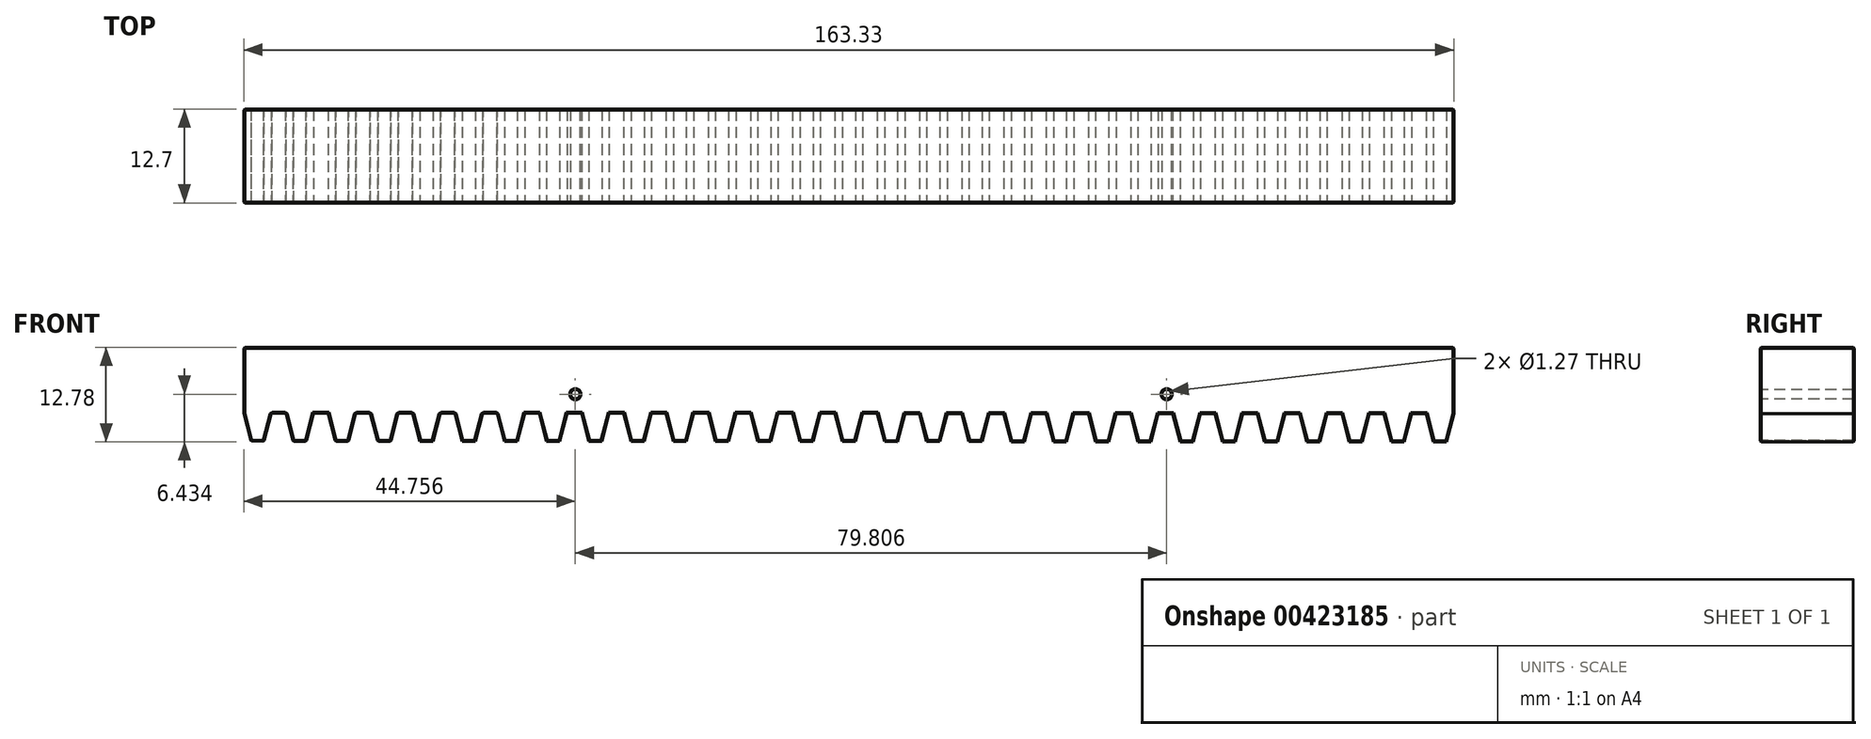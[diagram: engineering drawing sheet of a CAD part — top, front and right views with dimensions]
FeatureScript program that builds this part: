
annotation { "Feature Type Name" : "Feature", "Feature Type Description" : "" }
export const myFeature = defineFeature(function(context is Context, id is Id, definition is map)
    precondition{}
    {
        {
            var Q0;
            Q0=qCreatedBy(makeId("Front.planeOp"),FACE);
            var sketch = newSketch(context, id + "F0", { "sketchPlane" : qUnion([Q0])});
            skLineSegment(sketch, "E0.top", {"start": v(26.56, 6.35) * mm, "end": v(-136.77, 6.35) * mm});
            skLineSegment(sketch, "E0.left", {"start": v(152.4, -6.35) * mm, "end": v(152.4, 6.35) * mm});
            skLineSegment(sketch, "E1", {"start": v(-95.96, -15.55) * mm, "end": v(-95.96, -16.34) * mm});
            skLineSegment(sketch, "E2", {"start": v(-95.96, -16.34) * mm, "end": v(-95.96, -17.1) * mm});
            skLineSegment(sketch, "E3", {"start": v(-95.96, -17.1) * mm, "end": v(-96.35, -18.17) * mm});
            skLineSegment(sketch, "E4", {"start": v(-96.35, -18.17) * mm, "end": v(-96.56, -18.75) * mm});
            skLineSegment(sketch, "E5", {"start": v(-96.56, -18.75) * mm, "end": v(-97.98, -18.75) * mm});
            skLineSegment(sketch, "E6", {"start": v(-97.98, -18.75) * mm, "end": v(-98.54, -17.62) * mm});
            skLineSegment(sketch, "E7", {"start": v(-98.54, -17.62) * mm, "end": v(-98.72, -17.01) * mm});
            skLineSegment(sketch, "E8", {"start": v(-98.72, -17.01) * mm, "end": v(-98.73, -16.25) * mm});
            skLineSegment(sketch, "E9", {"start": v(-98.73, -16.25) * mm, "end": v(-98.73, -15.44) * mm});
            skLineSegment(sketch, "E10", {"start": v(-134.03, -6.35) * mm, "end": v(-133.05, -2.54) * mm});
            skLineSegment(sketch, "E11", {"start": v(-133.05, -2.54) * mm, "end": v(-131.07, -2.54) * mm});
            skLineSegment(sketch, "E12", {"start": v(-131.07, -2.54) * mm, "end": v(-130.09, -6.35) * mm});
            skLineSegment(sketch, "E13", {"start": v(-128.33, -6.37) * mm, "end": v(-127.35, -2.56) * mm});
            skLineSegment(sketch, "E14", {"start": v(-125.37, -2.56) * mm, "end": v(-124.39, -6.37) * mm});
            skLineSegment(sketch, "E15", {"start": v(-122.63, -6.37) * mm, "end": v(-121.65, -2.56) * mm});
            skLineSegment(sketch, "E16", {"start": v(-121.65, -2.56) * mm, "end": v(-119.67, -2.56) * mm});
            skLineSegment(sketch, "E17", {"start": v(-119.67, -2.56) * mm, "end": v(-118.69, -6.37) * mm});
            skLineSegment(sketch, "E18", {"start": v(-116.93, -6.37) * mm, "end": v(-115.95, -2.56) * mm});
            skLineSegment(sketch, "E19", {"start": v(-115.95, -2.56) * mm, "end": v(-113.97, -2.56) * mm});
            skLineSegment(sketch, "E20", {"start": v(-113.97, -2.56) * mm, "end": v(-112.99, -6.37) * mm});
            skLineSegment(sketch, "E21", {"start": v(-136.77, -2.56) * mm, "end": v(-135.8, -6.33) * mm});
            skLineSegment(sketch, "E22", {"start": v(-111.23, -6.37) * mm, "end": v(-110.25, -2.56) * mm});
            skLineSegment(sketch, "E23", {"start": v(-110.25, -2.56) * mm, "end": v(-108.28, -2.56) * mm});
            skLineSegment(sketch, "E24", {"start": v(-108.28, -2.56) * mm, "end": v(-107.3, -6.37) * mm});
            skLineSegment(sketch, "E25", {"start": v(-105.53, -6.37) * mm, "end": v(-104.55, -2.56) * mm});
            skLineSegment(sketch, "E26", {"start": v(-104.55, -2.56) * mm, "end": v(-102.58, -2.56) * mm});
            skLineSegment(sketch, "E27", {"start": v(-102.58, -2.56) * mm, "end": v(-101.6, -6.37) * mm});
            skLineSegment(sketch, "E28", {"start": v(-99.83, -6.37) * mm, "end": v(-98.85, -2.56) * mm});
            skLineSegment(sketch, "E29", {"start": v(-96.88, -2.56) * mm, "end": v(-95.9, -6.37) * mm});
            skLineSegment(sketch, "E30", {"start": v(-94.13, -6.37) * mm, "end": v(-93.15, -2.56) * mm});
            skLineSegment(sketch, "E31", {"start": v(-91.18, -2.56) * mm, "end": v(-90.2, -6.37) * mm});
            skLineSegment(sketch, "E32", {"start": v(-88.43, -6.37) * mm, "end": v(-87.45, -2.56) * mm});
            skLineSegment(sketch, "E33", {"start": v(-85.48, -2.56) * mm, "end": v(-84.5, -6.37) * mm});
            skLineSegment(sketch, "E34", {"start": v(-82.73, -6.39) * mm, "end": v(-81.75, -2.58) * mm});
            skLineSegment(sketch, "E35", {"start": v(-79.78, -2.58) * mm, "end": v(-78.8, -6.39) * mm});
            skLineSegment(sketch, "E36", {"start": v(-77.04, -6.37) * mm, "end": v(-76.05, -2.56) * mm});
            skLineSegment(sketch, "E37", {"start": v(-74.08, -2.56) * mm, "end": v(-73.1, -6.37) * mm});
            skLineSegment(sketch, "E38", {"start": v(-71.34, -6.37) * mm, "end": v(-70.35, -2.56) * mm});
            skLineSegment(sketch, "E39", {"start": v(-68.38, -2.56) * mm, "end": v(-67.4, -6.37) * mm});
            skLineSegment(sketch, "E40", {"start": v(-65.64, -6.37) * mm, "end": v(-64.65, -2.56) * mm});
            skLineSegment(sketch, "E41", {"start": v(-62.68, -2.56) * mm, "end": v(-61.7, -6.37) * mm});
            skLineSegment(sketch, "E42", {"start": v(-59.94, -6.37) * mm, "end": v(-58.95, -2.56) * mm});
            skLineSegment(sketch, "E43.trimOffspring", {"start": v(-124.4, -6.35) * mm, "end": v(-122.63, -6.35) * mm});
            skLineSegment(sketch, "E44.trimOffspring", {"start": v(-118.7, -6.35) * mm, "end": v(-116.93, -6.35) * mm});
            skLineSegment(sketch, "E45", {"start": v(-136.77, -2.56) * mm, "end": v(-136.77, 6.35) * mm});
            skLineSegment(sketch, "E46", {"start": v(-135.8, -6.33) * mm, "end": v(-134.03, -6.35) * mm});
            skLineSegment(sketch, "E47", {"start": v(-130.09, -6.35) * mm, "end": v(-128.33, -6.37) * mm});
            skLineSegment(sketch, "E48", {"start": v(-112.99, -6.37) * mm, "end": v(-111.23, -6.37) * mm});
            skLineSegment(sketch, "E49", {"start": v(-107.3, -6.37) * mm, "end": v(-105.53, -6.37) * mm});
            skLineSegment(sketch, "E50", {"start": v(-101.6, -6.37) * mm, "end": v(-99.83, -6.37) * mm});
            skLineSegment(sketch, "E51", {"start": v(-98.85, -2.56) * mm, "end": v(-96.88, -2.56) * mm});
            skLineSegment(sketch, "E52", {"start": v(-95.9, -6.37) * mm, "end": v(-94.13, -6.37) * mm});
            skLineSegment(sketch, "E53", {"start": v(-93.15, -2.56) * mm, "end": v(-91.18, -2.56) * mm});
            skLineSegment(sketch, "E54", {"start": v(-90.2, -6.37) * mm, "end": v(-88.43, -6.37) * mm});
            skLineSegment(sketch, "E55", {"start": v(-87.45, -2.56) * mm, "end": v(-85.48, -2.56) * mm});
            skLineSegment(sketch, "E56", {"start": v(-84.5, -6.37) * mm, "end": v(-82.73, -6.39) * mm});
            skLineSegment(sketch, "E57", {"start": v(-81.75, -2.58) * mm, "end": v(-79.78, -2.58) * mm});
            skLineSegment(sketch, "E58", {"start": v(-78.8, -6.39) * mm, "end": v(-77.04, -6.37) * mm});
            skLineSegment(sketch, "E59", {"start": v(-76.05, -2.56) * mm, "end": v(-74.08, -2.56) * mm});
            skLineSegment(sketch, "E60", {"start": v(-73.1, -6.37) * mm, "end": v(-71.34, -6.37) * mm});
            skLineSegment(sketch, "E61", {"start": v(-70.35, -2.56) * mm, "end": v(-68.38, -2.56) * mm});
            skLineSegment(sketch, "E62", {"start": v(-67.4, -6.37) * mm, "end": v(-65.64, -6.37) * mm});
            skLineSegment(sketch, "E63", {"start": v(-64.65, -2.56) * mm, "end": v(-62.68, -2.56) * mm});
            skLineSegment(sketch, "E64", {"start": v(-61.7, -6.37) * mm, "end": v(-59.94, -6.37) * mm});
            skLineSegment(sketch, "E65", {"start": v(-58.95, -2.56) * mm, "end": v(-56.98, -2.56) * mm});
            skLineSegment(sketch, "E66", {"start": v(-54.23, -6.38) * mm, "end": v(-53.24, -2.58) * mm});
            skLineSegment(sketch, "E67", {"start": v(-53.24, -2.58) * mm, "end": v(-51.27, -2.58) * mm});
            skLineSegment(sketch, "E68", {"start": v(-51.27, -2.58) * mm, "end": v(-50.28, -6.39) * mm});
            skLineSegment(sketch, "E69", {"start": v(-48.53, -6.4) * mm, "end": v(-47.54, -2.6) * mm});
            skLineSegment(sketch, "E70", {"start": v(-47.54, -2.6) * mm, "end": v(-45.57, -2.6) * mm});
            skLineSegment(sketch, "E71", {"start": v(-45.57, -2.6) * mm, "end": v(-44.58, -6.4) * mm});
            skLineSegment(sketch, "E72", {"start": v(-42.83, -6.4) * mm, "end": v(-41.84, -2.6) * mm});
            skLineSegment(sketch, "E73", {"start": v(-41.84, -2.6) * mm, "end": v(-39.87, -2.6) * mm});
            skLineSegment(sketch, "E74", {"start": v(-39.87, -2.6) * mm, "end": v(-38.88, -6.4) * mm});
            skLineSegment(sketch, "E75", {"start": v(-37.13, -6.4) * mm, "end": v(-36.14, -2.6) * mm});
            skLineSegment(sketch, "E76", {"start": v(-36.14, -2.6) * mm, "end": v(-34.17, -2.6) * mm});
            skLineSegment(sketch, "E77", {"start": v(-34.17, -2.6) * mm, "end": v(-33.18, -6.4) * mm});
            skLineSegment(sketch, "E78", {"start": v(-56.98, -2.56) * mm, "end": v(-56, -6.37) * mm});
            skLineSegment(sketch, "E79", {"start": v(-31.43, -6.4) * mm, "end": v(-30.44, -2.6) * mm});
            skLineSegment(sketch, "E80", {"start": v(-30.44, -2.6) * mm, "end": v(-28.47, -2.6) * mm});
            skLineSegment(sketch, "E81", {"start": v(-28.47, -2.6) * mm, "end": v(-27.48, -6.4) * mm});
            skLineSegment(sketch, "E82", {"start": v(-25.73, -6.4) * mm, "end": v(-24.74, -2.6) * mm});
            skLineSegment(sketch, "E83", {"start": v(-24.74, -2.6) * mm, "end": v(-22.77, -2.6) * mm});
            skLineSegment(sketch, "E84", {"start": v(-22.77, -2.6) * mm, "end": v(-21.78, -6.4) * mm});
            skLineSegment(sketch, "E85", {"start": v(-20.03, -6.4) * mm, "end": v(-19.04, -2.6) * mm});
            skLineSegment(sketch, "E86", {"start": v(-17.07, -2.6) * mm, "end": v(-16.08, -6.4) * mm});
            skLineSegment(sketch, "E87", {"start": v(-14.33, -6.4) * mm, "end": v(-13.34, -2.6) * mm});
            skLineSegment(sketch, "E88", {"start": v(-11.37, -2.6) * mm, "end": v(-10.38, -6.4) * mm});
            skLineSegment(sketch, "E89", {"start": v(-8.63, -6.4) * mm, "end": v(-7.64, -2.6) * mm});
            skLineSegment(sketch, "E90", {"start": v(-5.67, -2.6) * mm, "end": v(-4.68, -6.4) * mm});
            skLineSegment(sketch, "E91", {"start": v(-2.93, -6.42) * mm, "end": v(-1.94, -2.62) * mm});
            skLineSegment(sketch, "E92", {"start": v(0.03, -2.62) * mm, "end": v(1.01, -6.43) * mm});
            skLineSegment(sketch, "E93", {"start": v(2.77, -6.4) * mm, "end": v(3.76, -2.6) * mm});
            skLineSegment(sketch, "E94", {"start": v(5.73, -2.6) * mm, "end": v(6.71, -6.4) * mm});
            skLineSegment(sketch, "E95", {"start": v(8.47, -6.4) * mm, "end": v(9.46, -2.6) * mm});
            skLineSegment(sketch, "E96", {"start": v(11.43, -2.6) * mm, "end": v(12.41, -6.4) * mm});
            skLineSegment(sketch, "E97", {"start": v(14.17, -6.4) * mm, "end": v(15.16, -2.6) * mm});
            skLineSegment(sketch, "E98", {"start": v(17.13, -2.6) * mm, "end": v(18.11, -6.4) * mm});
            skLineSegment(sketch, "E99", {"start": v(19.87, -6.4) * mm, "end": v(20.85, -2.6) * mm});
            skLineSegment(sketch, "E100", {"start": v(22.83, -2.6) * mm, "end": v(23.81, -6.4) * mm});
            skLineSegment(sketch, "E101.trimOffspring", {"start": v(-44.59, -6.39) * mm, "end": v(-42.82, -6.39) * mm});
            skLineSegment(sketch, "E102.trimOffspring", {"start": v(-38.89, -6.39) * mm, "end": v(-37.12, -6.39) * mm});
            skLineSegment(sketch, "E103", {"start": v(-56, -6.37) * mm, "end": v(-54.23, -6.38) * mm});
            skLineSegment(sketch, "E104", {"start": v(-50.28, -6.39) * mm, "end": v(-48.53, -6.4) * mm});
            skLineSegment(sketch, "E105", {"start": v(-33.18, -6.4) * mm, "end": v(-31.43, -6.4) * mm});
            skLineSegment(sketch, "E106", {"start": v(-27.48, -6.4) * mm, "end": v(-25.73, -6.4) * mm});
            skLineSegment(sketch, "E107", {"start": v(-21.78, -6.4) * mm, "end": v(-20.03, -6.4) * mm});
            skLineSegment(sketch, "E108", {"start": v(-19.04, -2.6) * mm, "end": v(-17.07, -2.6) * mm});
            skLineSegment(sketch, "E109", {"start": v(-16.08, -6.4) * mm, "end": v(-14.33, -6.4) * mm});
            skLineSegment(sketch, "E110", {"start": v(-13.34, -2.6) * mm, "end": v(-11.37, -2.6) * mm});
            skLineSegment(sketch, "E111", {"start": v(-10.38, -6.4) * mm, "end": v(-8.63, -6.4) * mm});
            skLineSegment(sketch, "E112", {"start": v(-7.64, -2.6) * mm, "end": v(-5.67, -2.6) * mm});
            skLineSegment(sketch, "E113", {"start": v(-4.68, -6.4) * mm, "end": v(-2.93, -6.42) * mm});
            skLineSegment(sketch, "E114", {"start": v(-1.94, -2.62) * mm, "end": v(0.03, -2.62) * mm});
            skLineSegment(sketch, "E115", {"start": v(1.01, -6.43) * mm, "end": v(2.77, -6.4) * mm});
            skLineSegment(sketch, "E116", {"start": v(3.76, -2.6) * mm, "end": v(5.73, -2.6) * mm});
            skLineSegment(sketch, "E117", {"start": v(6.71, -6.4) * mm, "end": v(8.47, -6.4) * mm});
            skLineSegment(sketch, "E118", {"start": v(9.46, -2.6) * mm, "end": v(11.43, -2.6) * mm});
            skLineSegment(sketch, "E119", {"start": v(12.41, -6.4) * mm, "end": v(14.17, -6.4) * mm});
            skLineSegment(sketch, "E120", {"start": v(15.16, -2.6) * mm, "end": v(17.13, -2.6) * mm});
            skLineSegment(sketch, "E121", {"start": v(18.11, -6.4) * mm, "end": v(19.87, -6.4) * mm});
            skLineSegment(sketch, "E122", {"start": v(20.85, -2.6) * mm, "end": v(22.83, -2.6) * mm});
            skLineSegment(sketch, "E123", {"start": v(25.58, -6.42) * mm, "end": v(26.56, -2.61) * mm});
            skLineSegment(sketch, "E124", {"start": v(23.81, -6.4) * mm, "end": v(25.58, -6.42) * mm});
            skCircle(sketch, "E125", {"center": v(-92.01, 0) * mm, "radius": 0.64 * mm});
            skCircle(sketch, "E126", {"center": v(-12.2, 0) * mm, "radius": 0.64 * mm});
            skLineSegment(sketch, "E127", {"start": v(26.56, -2.61) * mm, "end": v(26.56, 6.35) * mm});
            skLineSegment(sketch, "E128", {"start": v(-127.35, -2.56) * mm, "end": v(-125.37, -2.56) * mm});
            skSolve(sketch);
        }
        {
            var Q0;
            Q0=makeQuery(id+"F0.imprint","IMPRINT",FACE,{"disambiguationData":[TD([[makeQuery(id+"F0.imprint","IMPRINT",EDGE,{"derivedFrom":sQuery(id+"F0.wireOp",EDGE,"E0.top")}),1.0]])]});
            extrude(context, id + "F1", {"entities" : qUnion([Q0]), "oppositeDirection" : true, "depth" : 12.7 * mm});
        }
        {
            var Q0;
            Q0=makeQuery(id+"F1.opExtrude","CAP_FACE",FACE,{"disambiguationData":[OSD([sQuery(id+"F0.wireOp",EDGE,"E0.top"),sQuery(id+"F0.wireOp",EDGE,"E10"),sQuery(id+"F0.wireOp",EDGE,"E11"),sQuery(id+"F0.wireOp",EDGE,"E12"),sQuery(id+"F0.wireOp",EDGE,"E13"),sQuery(id+"F0.wireOp",EDGE,"1db44ed7-9aab-4304-9b0a-d5fd72f29b89"),sQuery(id+"F0.wireOp",EDGE,"E14"),sQuery(id+"F0.wireOp",EDGE,"E15"),sQuery(id+"F0.wireOp",EDGE,"E16"),sQuery(id+"F0.wireOp",EDGE,"E17"),sQuery(id+"F0.wireOp",EDGE,"E18"),sQuery(id+"F0.wireOp",EDGE,"E19"),sQuery(id+"F0.wireOp",EDGE,"E20"),sQuery(id+"F0.wireOp",EDGE,"E21"),sQuery(id+"F0.wireOp",EDGE,"E22"),sQuery(id+"F0.wireOp",EDGE,"E23"),sQuery(id+"F0.wireOp",EDGE,"E24"),sQuery(id+"F0.wireOp",EDGE,"E25"),sQuery(id+"F0.wireOp",EDGE,"E26"),sQuery(id+"F0.wireOp",EDGE,"E27"),sQuery(id+"F0.wireOp",EDGE,"E28"),sQuery(id+"F0.wireOp",EDGE,"d0c50af5-ac39-4cf5-90a2-4504431eaded"),sQuery(id+"F0.wireOp",EDGE,"E29"),sQuery(id+"F0.wireOp",EDGE,"E30"),sQuery(id+"F0.wireOp",EDGE,"e7b25a4d-063f-46ac-9386-bb0dd44a16b1"),sQuery(id+"F0.wireOp",EDGE,"E31"),sQuery(id+"F0.wireOp",EDGE,"E32"),sQuery(id+"F0.wireOp",EDGE,"54059590-1058-411a-a35c-84b59182508d"),sQuery(id+"F0.wireOp",EDGE,"E33"),sQuery(id+"F0.wireOp",EDGE,"E34"),sQuery(id+"F0.wireOp",EDGE,"8aab2b11-0095-4644-a401-248724ba89be"),sQuery(id+"F0.wireOp",EDGE,"E35"),sQuery(id+"F0.wireOp",EDGE,"E36"),sQuery(id+"F0.wireOp",EDGE,"c960a415-8344-4536-8b53-73d4f96e9fdc"),sQuery(id+"F0.wireOp",EDGE,"E37"),sQuery(id+"F0.wireOp",EDGE,"E38"),sQuery(id+"F0.wireOp",EDGE,"62d0bbd9-5977-49a0-9980-fbc7ca1cb1f4"),sQuery(id+"F0.wireOp",EDGE,"E39"),sQuery(id+"F0.wireOp",EDGE,"E40"),sQuery(id+"F0.wireOp",EDGE,"4fefa8e7-a774-4dae-be22-217b66629c21"),sQuery(id+"F0.wireOp",EDGE,"E41"),sQuery(id+"F0.wireOp",EDGE,"E42"),sQuery(id+"F0.wireOp",EDGE,"bb5a2345-079d-430a-8205-bbfcd13575cd"),sQuery(id+"F0.wireOp",EDGE,"61ae00f4-fc72-44b3-ad8d-509071cab8c4"),sQuery(id+"F0.wireOp",EDGE,"f98411e8-25a9-4283-a79b-aa8ad212dbc6"),sQuery(id+"F0.wireOp",EDGE,"E43.trimOffspring"),sQuery(id+"F0.wireOp",EDGE,"E44.trimOffspring"),sQuery(id+"F0.wireOp",EDGE,"dac8fa4d-72e7-4378-9e42-cf47ebc63217.trimOffspring"),sQuery(id+"F0.wireOp",EDGE,"7b59f605-3025-43fb-bbdd-bbc57b71cc2b.trimOffspring"),sQuery(id+"F0.wireOp",EDGE,"33b95fc1-906c-4fb0-830d-551110b9f39b.trimOffspring"),sQuery(id+"F0.wireOp",EDGE,"57e515cb-325b-4a66-b09a-3791c6e28d7d.trimOffspring"),sQuery(id+"F0.wireOp",EDGE,"00886d8f-4349-45f1-959c-160f4e5e0cad.trimOffspring"),sQuery(id+"F0.wireOp",EDGE,"00735235-d0f1-4db2-a406-7b14ad57794c.trimOffspring"),sQuery(id+"F0.wireOp",EDGE,"588f8932-8913-408c-8446-e06310ac0838.trimOffspring"),sQuery(id+"F0.wireOp",EDGE,"bbaf20a5-4e78-4d06-9bde-ea2d9a00ea50.trimOffspring"),sQuery(id+"F0.wireOp",EDGE,"20fd09fb-2384-4b3c-8516-cf38eb0e431c.trimOffspring"),sQuery(id+"F0.wireOp",EDGE,"908e19e9-25ab-44f4-a599-a66f89f58b28.trimOffspring"),sQuery(id+"F0.wireOp",EDGE,"5fdcf918-9551-469f-9cc3-b51603cfebde.trimOffspring"),sQuery(id+"F0.wireOp",EDGE,"E45"),sQuery(id+"F0.wireOp",EDGE,"MubH7WfP-UBmi-4eHw-NPtt-TXrD7jQMshnV"),sQuery(id+"F0.wireOp",EDGE,"E46"),sQuery(id+"F0.wireOp",EDGE,"E47")])],"isStart":true});
            var Q1;
            Q1=makeQuery(id+"F1.opExtrude","CAP_FACE",FACE,{"disambiguationData":[OSD([sQuery(id+"F0.wireOp",EDGE,"E0.top"),sQuery(id+"F0.wireOp",EDGE,"E10"),sQuery(id+"F0.wireOp",EDGE,"E11"),sQuery(id+"F0.wireOp",EDGE,"E12"),sQuery(id+"F0.wireOp",EDGE,"E13"),sQuery(id+"F0.wireOp",EDGE,"1db44ed7-9aab-4304-9b0a-d5fd72f29b89"),sQuery(id+"F0.wireOp",EDGE,"E14"),sQuery(id+"F0.wireOp",EDGE,"E15"),sQuery(id+"F0.wireOp",EDGE,"E16"),sQuery(id+"F0.wireOp",EDGE,"E17"),sQuery(id+"F0.wireOp",EDGE,"E18"),sQuery(id+"F0.wireOp",EDGE,"E19"),sQuery(id+"F0.wireOp",EDGE,"E20"),sQuery(id+"F0.wireOp",EDGE,"E21"),sQuery(id+"F0.wireOp",EDGE,"E22"),sQuery(id+"F0.wireOp",EDGE,"E23"),sQuery(id+"F0.wireOp",EDGE,"E24"),sQuery(id+"F0.wireOp",EDGE,"E25"),sQuery(id+"F0.wireOp",EDGE,"E26"),sQuery(id+"F0.wireOp",EDGE,"E27"),sQuery(id+"F0.wireOp",EDGE,"E28"),sQuery(id+"F0.wireOp",EDGE,"d0c50af5-ac39-4cf5-90a2-4504431eaded"),sQuery(id+"F0.wireOp",EDGE,"E29"),sQuery(id+"F0.wireOp",EDGE,"E30"),sQuery(id+"F0.wireOp",EDGE,"e7b25a4d-063f-46ac-9386-bb0dd44a16b1"),sQuery(id+"F0.wireOp",EDGE,"E31"),sQuery(id+"F0.wireOp",EDGE,"E32"),sQuery(id+"F0.wireOp",EDGE,"54059590-1058-411a-a35c-84b59182508d"),sQuery(id+"F0.wireOp",EDGE,"E33"),sQuery(id+"F0.wireOp",EDGE,"E34"),sQuery(id+"F0.wireOp",EDGE,"8aab2b11-0095-4644-a401-248724ba89be"),sQuery(id+"F0.wireOp",EDGE,"E35"),sQuery(id+"F0.wireOp",EDGE,"E36"),sQuery(id+"F0.wireOp",EDGE,"c960a415-8344-4536-8b53-73d4f96e9fdc"),sQuery(id+"F0.wireOp",EDGE,"E37"),sQuery(id+"F0.wireOp",EDGE,"E38"),sQuery(id+"F0.wireOp",EDGE,"62d0bbd9-5977-49a0-9980-fbc7ca1cb1f4"),sQuery(id+"F0.wireOp",EDGE,"E39"),sQuery(id+"F0.wireOp",EDGE,"E40"),sQuery(id+"F0.wireOp",EDGE,"4fefa8e7-a774-4dae-be22-217b66629c21"),sQuery(id+"F0.wireOp",EDGE,"E41"),sQuery(id+"F0.wireOp",EDGE,"E42"),sQuery(id+"F0.wireOp",EDGE,"bb5a2345-079d-430a-8205-bbfcd13575cd"),sQuery(id+"F0.wireOp",EDGE,"61ae00f4-fc72-44b3-ad8d-509071cab8c4"),sQuery(id+"F0.wireOp",EDGE,"f98411e8-25a9-4283-a79b-aa8ad212dbc6"),sQuery(id+"F0.wireOp",EDGE,"E43.trimOffspring"),sQuery(id+"F0.wireOp",EDGE,"E44.trimOffspring"),sQuery(id+"F0.wireOp",EDGE,"dac8fa4d-72e7-4378-9e42-cf47ebc63217.trimOffspring"),sQuery(id+"F0.wireOp",EDGE,"7b59f605-3025-43fb-bbdd-bbc57b71cc2b.trimOffspring"),sQuery(id+"F0.wireOp",EDGE,"33b95fc1-906c-4fb0-830d-551110b9f39b.trimOffspring"),sQuery(id+"F0.wireOp",EDGE,"57e515cb-325b-4a66-b09a-3791c6e28d7d.trimOffspring"),sQuery(id+"F0.wireOp",EDGE,"00886d8f-4349-45f1-959c-160f4e5e0cad.trimOffspring"),sQuery(id+"F0.wireOp",EDGE,"00735235-d0f1-4db2-a406-7b14ad57794c.trimOffspring"),sQuery(id+"F0.wireOp",EDGE,"588f8932-8913-408c-8446-e06310ac0838.trimOffspring"),sQuery(id+"F0.wireOp",EDGE,"bbaf20a5-4e78-4d06-9bde-ea2d9a00ea50.trimOffspring"),sQuery(id+"F0.wireOp",EDGE,"20fd09fb-2384-4b3c-8516-cf38eb0e431c.trimOffspring"),sQuery(id+"F0.wireOp",EDGE,"908e19e9-25ab-44f4-a599-a66f89f58b28.trimOffspring"),sQuery(id+"F0.wireOp",EDGE,"5fdcf918-9551-469f-9cc3-b51603cfebde.trimOffspring"),sQuery(id+"F0.wireOp",EDGE,"E45"),sQuery(id+"F0.wireOp",EDGE,"MubH7WfP-UBmi-4eHw-NPtt-TXrD7jQMshnV"),sQuery(id+"F0.wireOp",EDGE,"E46"),sQuery(id+"F0.wireOp",EDGE,"E47")])],"isStart":false});
            var Q2;
            Q2=makeQuery(id+"F1.opExtrude","SWEPT_FACE",FACE,{"disambiguationData":[OSD([sQuery(id+"F0.wireOp",EDGE,"MubH7WfP-UBmi-4eHw-NPtt-TXrD7jQMshnV")])]});
            var Q3;
            Q3=makeQuery(id+"F1.opExtrude","SWEPT_FACE",FACE,{"disambiguationData":[OSD([sQuery(id+"F0.wireOp",EDGE,"E0.top")])]});
            var Q4;
            Q4=makeQuery(id+"F1.opExtrude","SWEPT_FACE",FACE,{"disambiguationData":[OSD([sQuery(id+"F0.wireOp",EDGE,"E45")])]});
            var Q5;
            Q5=makeQuery(id+"F1.opExtrude","SWEPT_FACE",FACE,{"disambiguationData":[OSD([sQuery(id+"F0.wireOp",EDGE,"E46")])]});
            var Q6;
            Q6=makeQuery(id+"F1.opExtrude","SWEPT_FACE",FACE,{"disambiguationData":[OSD([sQuery(id+"F0.wireOp",EDGE,"E11")])]});
            var Q7;
            Q7=makeQuery(id+"F1.opExtrude","SWEPT_FACE",FACE,{"disambiguationData":[OSD([sQuery(id+"F0.wireOp",EDGE,"E47")])]});
            var Q8;
            Q8=makeQuery(id+"F1.opExtrude","SWEPT_FACE",FACE,{"disambiguationData":[OSD([sQuery(id+"F0.wireOp",EDGE,"1db44ed7-9aab-4304-9b0a-d5fd72f29b89")])]});
            var Q9;
            Q9=makeQuery(id+"F1.opExtrude","SWEPT_FACE",FACE,{"disambiguationData":[OSD([sQuery(id+"F0.wireOp",EDGE,"E43.trimOffspring")])]});
            var Q10;
            Q10=makeQuery(id+"F1.opExtrude","SWEPT_FACE",FACE,{"disambiguationData":[OSD([sQuery(id+"F0.wireOp",EDGE,"E16")])]});
            var Q11;
            Q11=makeQuery(id+"F1.opExtrude","SWEPT_FACE",FACE,{"disambiguationData":[OSD([sQuery(id+"F0.wireOp",EDGE,"E44.trimOffspring")])]});
            var Q12;
            Q12=makeQuery(id+"F1.opExtrude","SWEPT_FACE",FACE,{"disambiguationData":[OSD([sQuery(id+"F0.wireOp",EDGE,"E19")])]});
            var Q13;
            Q13=makeQuery(id+"F1.opExtrude","SWEPT_FACE",FACE,{"disambiguationData":[OSD([sQuery(id+"F0.wireOp",EDGE,"dac8fa4d-72e7-4378-9e42-cf47ebc63217.trimOffspring")])]});
            var Q14;
            Q14=makeQuery(id+"F1.opExtrude","SWEPT_EDGE",EDGE,{"disambiguationData":[OSD([sQuery(id+"F0.wireOp",EDGE,"E22"),sQuery(id+"F0.wireOp",EDGE,"E23")])]});
            var Q15;
            Q15=makeQuery(id+"F1.opExtrude","SWEPT_FACE",FACE,{"disambiguationData":[OSD([sQuery(id+"F0.wireOp",EDGE,"E23")])]});
            var Q16;
            Q16=makeQuery(id+"F1.opExtrude","SWEPT_FACE",FACE,{"disambiguationData":[OSD([sQuery(id+"F0.wireOp",EDGE,"7b59f605-3025-43fb-bbdd-bbc57b71cc2b.trimOffspring")])]});
            var Q17;
            Q17=makeQuery(id+"F1.opExtrude","SWEPT_FACE",FACE,{"disambiguationData":[OSD([sQuery(id+"F0.wireOp",EDGE,"E26")])]});
            var Q18;
            Q18=makeQuery(id+"F1.opExtrude","SWEPT_FACE",FACE,{"disambiguationData":[OSD([sQuery(id+"F0.wireOp",EDGE,"33b95fc1-906c-4fb0-830d-551110b9f39b.trimOffspring")])]});
            var Q19;
            Q19=makeQuery(id+"F1.opExtrude","SWEPT_FACE",FACE,{"disambiguationData":[OSD([sQuery(id+"F0.wireOp",EDGE,"d0c50af5-ac39-4cf5-90a2-4504431eaded")])]});
            var Q20;
            Q20=makeQuery(id+"F1.opExtrude","SWEPT_FACE",FACE,{"disambiguationData":[OSD([sQuery(id+"F0.wireOp",EDGE,"57e515cb-325b-4a66-b09a-3791c6e28d7d.trimOffspring")])]});
            var Q21;
            Q21=makeQuery(id+"F1.opExtrude","SWEPT_FACE",FACE,{"disambiguationData":[OSD([sQuery(id+"F0.wireOp",EDGE,"00886d8f-4349-45f1-959c-160f4e5e0cad.trimOffspring")])]});
            var Q22;
            Q22=makeQuery(id+"F1.opExtrude","SWEPT_FACE",FACE,{"disambiguationData":[OSD([sQuery(id+"F0.wireOp",EDGE,"54059590-1058-411a-a35c-84b59182508d")])]});
            chamfer(context, id + "F2", {"entities" : qUnion([Q0, Q1, Q2, Q3, Q4, Q5, Q6, Q7, Q8, Q9, Q10, Q11, Q12, Q13, Q14, Q15, Q16, Q17, Q18, Q19, Q20, Q21, Q22]), "width" : 0.13 * mm, "tangentPropagation" : true});
        }
    });
